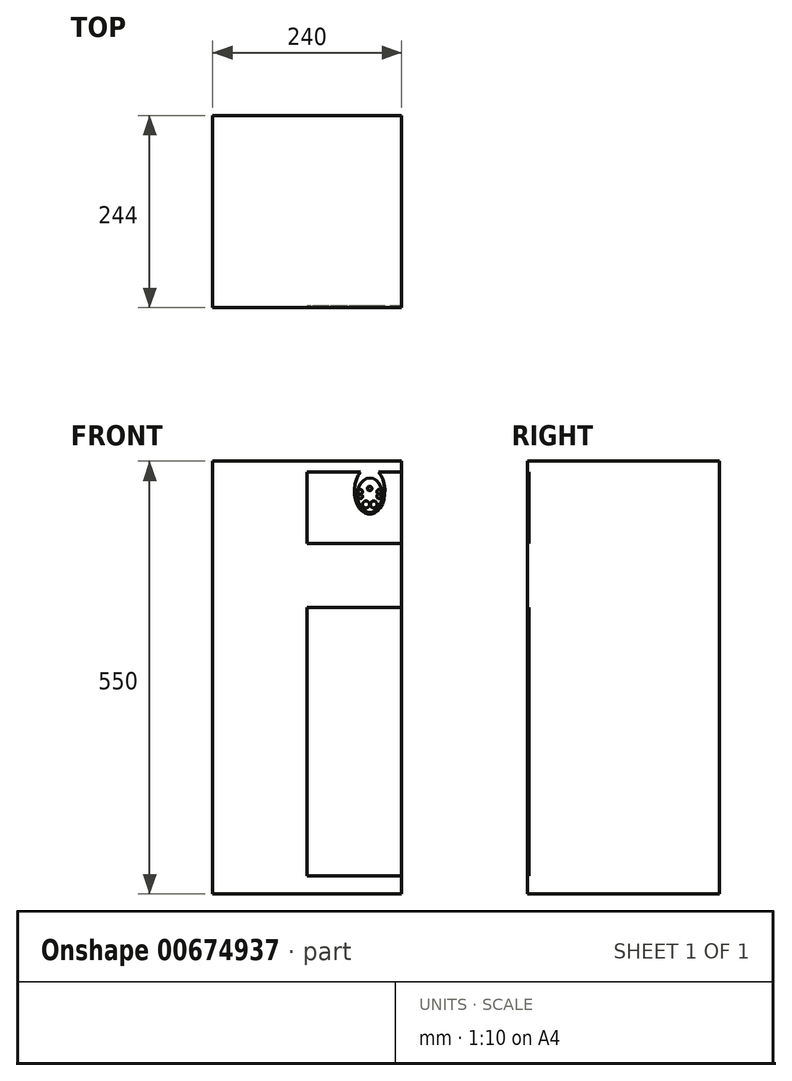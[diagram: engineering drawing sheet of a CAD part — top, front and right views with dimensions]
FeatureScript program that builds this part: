
annotation { "Feature Type Name" : "Feature", "Feature Type Description" : "" }
export const myFeature = defineFeature(function(context is Context, id is Id, definition is map)
    precondition{}
    {
        {
            var Q0;
            Q0=qCreatedBy(makeId("Front.planeOp"),FACE);
            var sketch = newSketch(context, id + "F0", { "sketchPlane" : qUnion([Q0])});
            skLineSegment(sketch, "E0.bottom", {"start": v(120, 275) * mm, "end": v(-120, 275) * mm});
            skLineSegment(sketch, "E0.top", {"start": v(120, -275) * mm, "end": v(-120, -275) * mm});
            skLineSegment(sketch, "E0.left", {"start": v(120, 275) * mm, "end": v(120, -275) * mm});
            skLineSegment(sketch, "E0.right", {"start": v(-120, 275) * mm, "end": v(-120, -275) * mm});
            skPoint(sketch, "E0.middle", {"position": v(0, 0) * mm});
            skSolve(sketch);
        }
        {
            var Q0;
            Q0=makeQuery(id+"F0.imprint","IMPRINT",FACE,{"disambiguationData":[TD([[makeQuery(id+"F0.imprint","IMPRINT",EDGE,{"derivedFrom":sQuery(id+"F0.wireOp",EDGE,"E0.bottom")}),1.0]])]});
            extrude(context, id + "F1", {"entities" : qUnion([Q0]), "depth" : 244 * mm, "offsetDistance" : 25 * mm});
        }
        {
            var Q0;
            Q0=makeQuery(id+"F1.opExtrude","CAP_FACE",FACE,{"disambiguationData":[OSD([sQuery(id+"F0.wireOp",EDGE,"E0.bottom"),sQuery(id+"F0.wireOp",EDGE,"E0.top"),sQuery(id+"F0.wireOp",EDGE,"E0.left"),sQuery(id+"F0.wireOp",EDGE,"E0.right")])],"isStart":false});
            var sketch = newSketch(context, id + "F2", { "sketchPlane" : qUnion([Q0])});
            skEllipse(sketch, "E1", {"center": v(79.64, 231.57) * mm, "majorRadius": 21.83 * mm, "minorRadius": 16.04 * mm, "majorAxis": v(0, 1)});
            skEllipse(sketch, "E2", {"center": v(79.36, 237.22) * mm, "majorRadius": 29.93 * mm, "minorRadius": 19.27 * mm, "majorAxis": v(0, 1)});
            skCircle(sketch, "E3", {"center": v(74.76, 219.83) * mm, "radius": 4.32 * mm});
            skCircle(sketch, "E4.MirrorC", {"center": v(84.52, 219.83) * mm, "radius": 4.32 * mm});
            skCircle(sketch, "E5", {"center": v(67.51, 230.1) * mm, "radius": 2.8 * mm});
            skCircle(sketch, "E6.MirrorC", {"center": v(67.51, 236.08) * mm, "radius": 2.8 * mm});
            skCircle(sketch, "E7.MirrorC", {"center": v(91.22, 230.1) * mm, "radius": 2.8 * mm});
            skCircle(sketch, "E8.MirrorC", {"center": v(91.22, 236.08) * mm, "radius": 2.8 * mm});
            skCircle(sketch, "E9", {"center": v(79.36, 240.12) * mm, "radius": 2.85 * mm});
            skLineSegment(sketch, "E10", {"start": v(0, 89.19) * mm, "end": v(120, 89.19) * mm});
            skLineSegment(sketch, "E11.bottom", {"start": v(120, 261.37) * mm, "end": v(0, 261.37) * mm});
            skLineSegment(sketch, "E11.top", {"start": v(120, 170.55) * mm, "end": v(0, 170.55) * mm});
            skLineSegment(sketch, "E11.left", {"start": v(120, 261.37) * mm, "end": v(120, 170.55) * mm});
            skLineSegment(sketch, "E11.right", {"start": v(0, 261.37) * mm, "end": v(0, 170.55) * mm});
            skLineSegment(sketch, "E12.bottom", {"start": v(0, 170.55) * mm, "end": v(120, 170.55) * mm});
            skLineSegment(sketch, "E12.top", {"start": v(0, -251.77) * mm, "end": v(120, -251.77) * mm});
            skLineSegment(sketch, "E12.left", {"start": v(0, 89.19) * mm, "end": v(0, -251.77) * mm});
            skLineSegment(sketch, "E12.right", {"start": v(120, 170.55) * mm, "end": v(120, -251.77) * mm});
            skSolve(sketch);
        }
        {
            var Q0;
            Q0=makeQuery(id+"F2.imprint","IMPRINT",FACE,{"disambiguationData":[TD([[makeQuery(id+"F2.imprint","IMPRINT",EDGE,{"derivedFrom":sQuery(id+"F2.wireOp",EDGE,"E1")}),1.0]])]});
            var Q1;
            Q1=makeQuery(id+"F2.imprint","IMPRINT",FACE,{"disambiguationData":[TD([[makeQuery(id+"F2.imprint","IMPRINT",EDGE,{"derivedFrom":sQuery(id+"F2.wireOp",EDGE,"E11.top")}),-1.0]])]});
            var Q2;
            {var subQ0=sQuery(id+"F2.wireOp",EDGE,"E11.left");Q2=makeQuery(id+"F2.imprint","IMPRINT",FACE,{"disambiguationData":[TD([[makeQuery(id+"F2.imprint","IMPRINT",EDGE,{"derivedFrom":subQ0}),-1.0]])]});}
            var Q3;
            {var subQ0=sQuery(id+"F2.wireOp",EDGE,"E10");Q3=makeQuery(id+"F2.imprint","IMPRINT",FACE,{"disambiguationData":[TD([[makeQuery(id+"F2.imprint","IMPRINT",EDGE,{"derivedFrom":subQ0}),-1.0]])]});}
            extrude(context, id + "F3", {"entities" : qUnion([Q0, Q1, Q2, Q3]), "operationType" : NewBodyOperationType.REMOVE, "oppositeDirection" : true, "depth" : 2 * mm, "offsetDistance" : 25 * mm});
        }
    });
